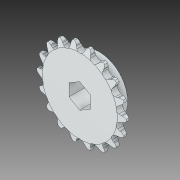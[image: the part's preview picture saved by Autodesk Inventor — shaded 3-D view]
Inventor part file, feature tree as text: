
AUTODESK INVENTOR PART (.ipt)
format: ipt  version: 2019 (Build 230136000, 136)  size: 525,824 bytes
history: native  units: in
note: dims shown in document units (in); Inventor stores cm internally (conversion verified against a paired STEP export)
features: chamfer x1
ambient origin geometry x8: Origin, YZ Plane, XZ Plane, XY Plane, X Axis, Y Axis, Z Axis, Center Point
bodies: Solid1 (feature_tree)
feature tree (1):
  chamfer  "Chamfer2"  [1 undecoded]
note: 1 required parameter value undecoded (feature->parameter linkage not recoverable at this tier; creation-order binding heuristic only, values carry confidence <= 0.55)
